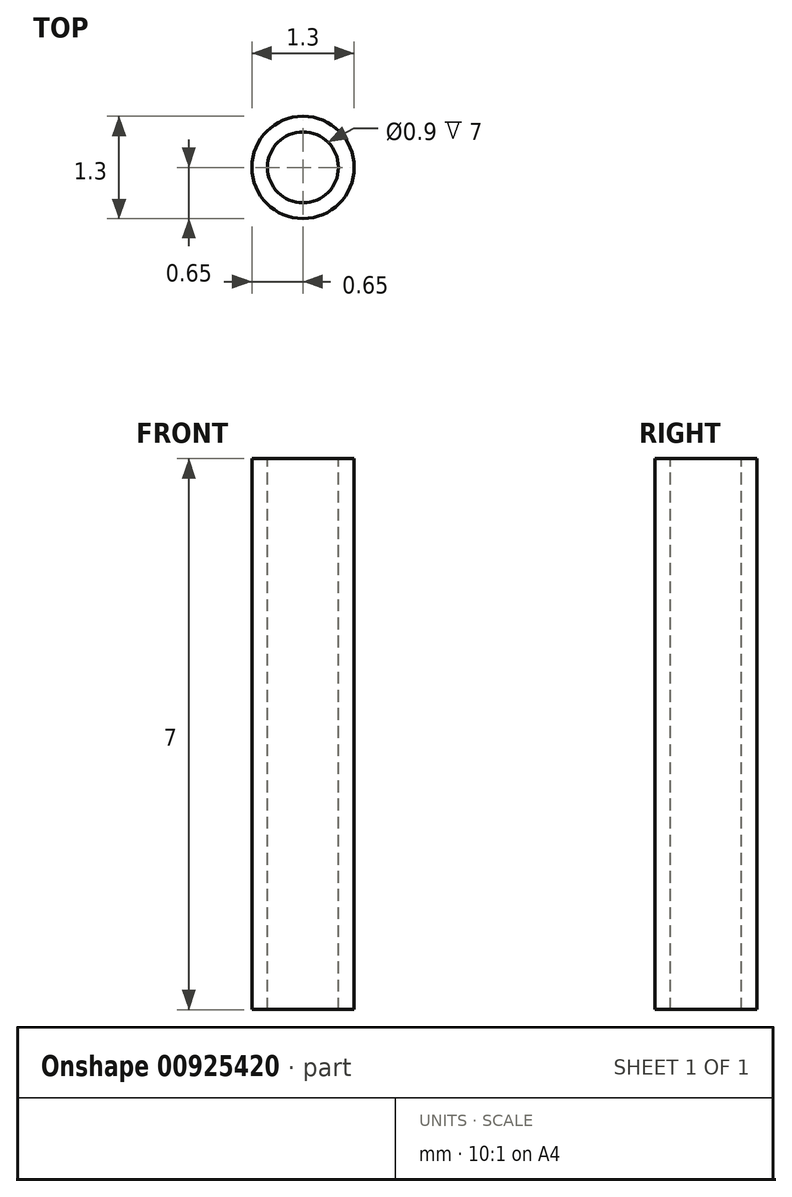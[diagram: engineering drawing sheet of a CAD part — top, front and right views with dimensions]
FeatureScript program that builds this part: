
annotation { "Feature Type Name" : "Feature", "Feature Type Description" : "" }
export const myFeature = defineFeature(function(context is Context, id is Id, definition is map)
    precondition{}
    {
        {
            var Q0;
            Q0=qCreatedBy(makeId("Front.planeOp"),FACE);
            var sketch = newSketch(context, id + "F0", { "sketchPlane" : qUnion([Q0])});
            skLineSegment(sketch, "E0", {"start": v(0, 2.48) * mm, "end": v(0, -2.84) * mm, "construction": true});
            skLineSegment(sketch, "E1", {"start": v(-0.65, 4.24) * mm, "end": v(-0.65, -2.76) * mm});
            skLineSegment(sketch, "E2", {"start": v(-0.65, -2.76) * mm, "end": v(-0.45, -2.76) * mm});
            skLineSegment(sketch, "E3", {"start": v(-0.45, -2.76) * mm, "end": v(-0.45, 4.24) * mm});
            skLineSegment(sketch, "E4", {"start": v(-0.45, 4.24) * mm, "end": v(-0.65, 4.24) * mm});
            skSolve(sketch);
        }
        {
            var Q0;
            Q0 = qSketchRegion(id + "F0", true);
            var Q1;
            Q1=sQuery(id+"F0.wireOp",EDGE,"E0");
            revolve(context, id + "F1", {"surfaceOperationType" : NewSurfaceOperationType.NEW, "entities" : qUnion([Q0]), "axis" : qUnion([Q1]), "revolveType" : RevolveType.FULL});
        }
    });
